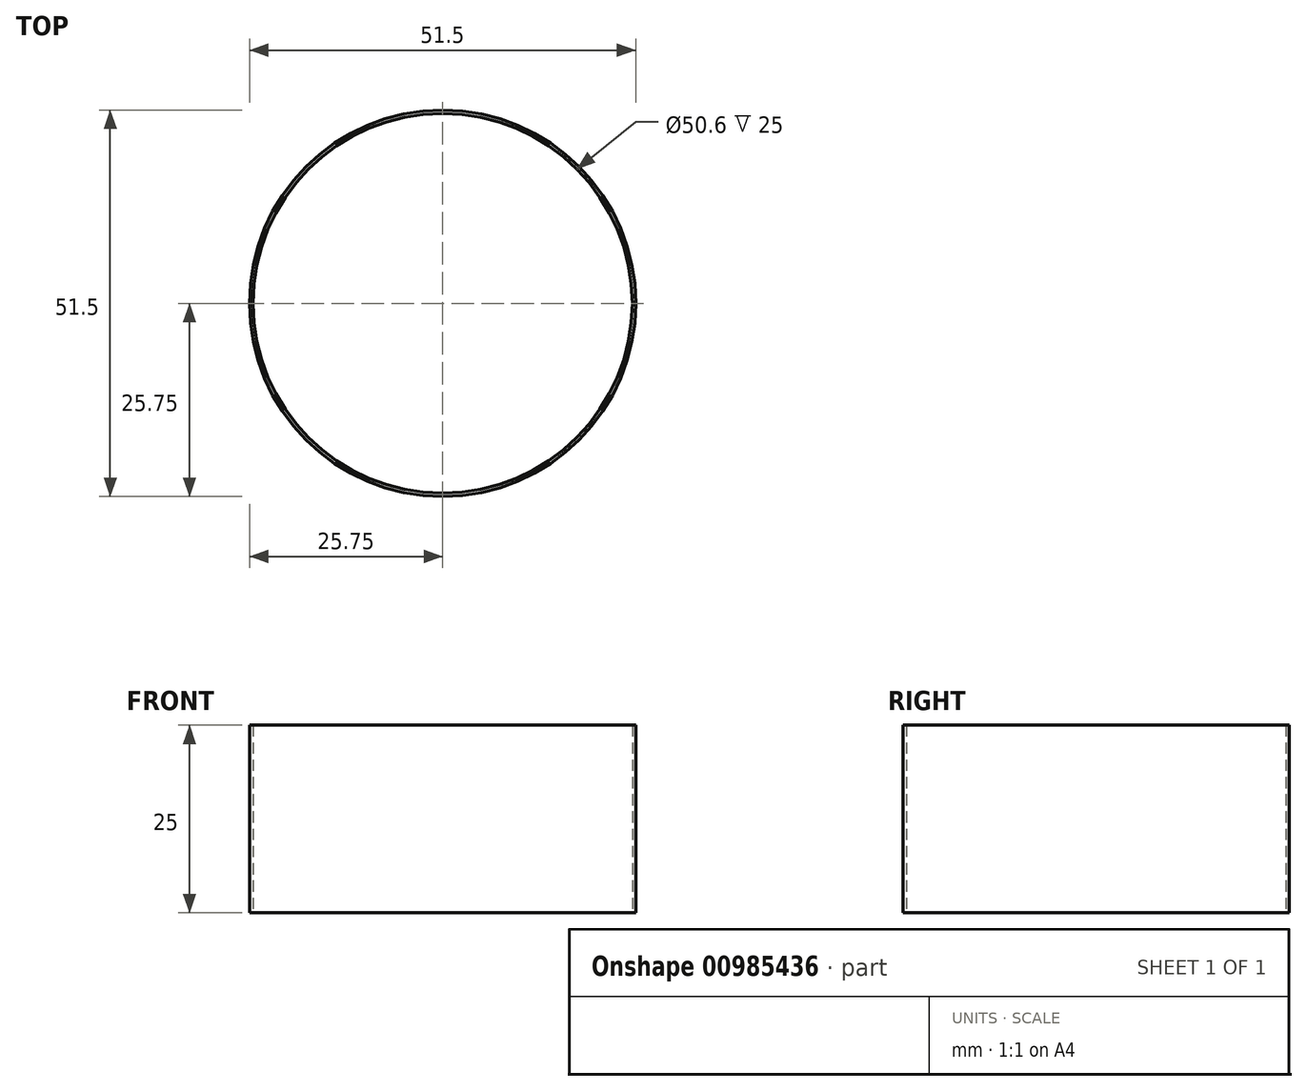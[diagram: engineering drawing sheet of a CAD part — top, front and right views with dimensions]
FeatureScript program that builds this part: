
annotation { "Feature Type Name" : "Feature", "Feature Type Description" : "" }
export const myFeature = defineFeature(function(context is Context, id is Id, definition is map)
    precondition{}
    {
        {
            var Q0;
            Q0=qCreatedBy(makeId("Top.planeOp"),FACE);
            var sketch = newSketch(context, id + "F0", { "sketchPlane" : qUnion([Q0])});
            skCircle(sketch, "E0", {"center": v(0, 0) * mm, "radius": 25.75 * mm});
            skCircle(sketch, "E1", {"center": v(0, 0) * mm, "radius": 25.3 * mm});
            skSolve(sketch);
        }
        {
            var Q0;
            Q0=makeQuery(id+"F0.imprint","IMPRINT",FACE,{"disambiguationData":[TD([[makeQuery(id+"F0.imprint","IMPRINT",EDGE,{"derivedFrom":sQuery(id+"F0.wireOp",EDGE,"E0")}),1.0]])]});
            extrude(context, id + "F1", {"entities" : qUnion([Q0]), "depth" : 25 * mm, "offsetDistance" : 25 * mm});
        }
    });
